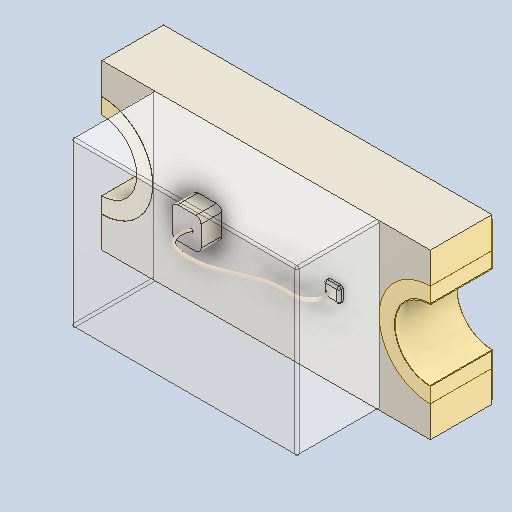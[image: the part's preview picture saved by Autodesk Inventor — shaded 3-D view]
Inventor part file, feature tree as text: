
AUTODESK INVENTOR PART (.ipt)
format: ipt  version: 2024 (Build 280153000, 153)  size: 231,936 bytes
history: native  units: in
note: dims shown in document units (in); Inventor stores cm internally (conversion verified against a paired STEP export)
features: mirror x3, fillet x2, other x1, sweep x1
ambient origin geometry x8: Origin, YZ Plane, XZ Plane, XY Plane, X Axis, Y Axis, Z Axis, Center Point
bodies: Solid1 (feature_tree), Solid2 (feature_tree), Solid3 (feature_tree), Solid4 (feature_tree), Solid5 (feature_tree), Solid6 (feature_tree), Solid7 (feature_tree)
feature tree (7):
  mirror  "Mirror1[1]"
  mirror  "Mirror1[3]"
  mirror  "Mirror1[4]"
  other  "Boss-Extrude5"
  fillet  "Fillet1"  [1 undecoded]
  sweep  "Sweep2"
  fillet  "Fillet2"  [1 undecoded]
note: 2 required parameter values undecoded (feature->parameter linkage not recoverable at this tier; creation-order binding heuristic only, values carry confidence <= 0.55)
